FCSTD DOCUMENT  (FreeCAD 0.20R29177 (Git))
Label: Xpad_Top
License: All rights reserved
LicenseURL: http://en.wikipedia.org/wiki/All_rights_reserved
objects: Sketcher::SketchObject×1
note: 1 computed .brp shape members not serialized (recipe doc carries the construction recipe); baked Part::Feature solids carry a one-line shape summary decoded from their .brp

FEATURE [Sketcher::SketchObject] Sketch
  FullyConstrained = false
  sketch-geometry (36):
    g0: LineSegment StartX=0 StartY=47.625 StartZ=0 EndX=141.287 EndY=47.625 EndZ=0
    g1: LineSegment StartX=141.287 StartY=47.625 StartZ=0 EndX=141.287 EndY=0 EndZ=0
    g2: LineSegment StartX=141.287 StartY=0 StartZ=0 EndX=0 EndY=0 EndZ=0
    g3: LineSegment StartX=0 StartY=0 StartZ=0 EndX=0 EndY=47.625 EndZ=0
    g4: Circle CenterX=3.175 CenterY=3.175 CenterZ=0 NormalX=0 NormalY=0 NormalZ=1 AngleXU=0 Radius=1.5875
    g5: Circle CenterX=138.113 CenterY=3.175 CenterZ=0 NormalX=0 NormalY=0 NormalZ=1 AngleXU=0 Radius=1.5875
    g6: Circle CenterX=138.113 CenterY=44.45 CenterZ=0 NormalX=0 NormalY=0 NormalZ=1 AngleXU=0 Radius=1.5875
    g7: Circle CenterX=3.175 CenterY=44.45 CenterZ=0 NormalX=0 NormalY=0 NormalZ=1 AngleXU=0 Radius=1.5875
    g8: LineSegment StartX=1.90416 StartY=41.4018 StartZ=0 EndX=4.17658 EndY=41.4018 EndZ=0
    g9: LineSegment StartX=4.17658 StartY=41.4018 StartZ=0 EndX=4.17658 EndY=6.17209 EndZ=0
    g10: LineSegment StartX=4.17658 StartY=6.17209 StartZ=0 EndX=1.90416 EndY=6.17209 EndZ=0
    g11: LineSegment StartX=1.90416 StartY=6.17209 StartZ=0 EndX=1.90416 EndY=41.4018 EndZ=0
    g12: LineSegment StartX=136.92 StartY=40.3737 StartZ=0 EndX=139.308 EndY=40.3737 EndZ=0
    g13: LineSegment StartX=139.308 StartY=40.3737 StartZ=0 EndX=139.308 EndY=6.45346 EndZ=0
    g14: LineSegment StartX=139.308 StartY=6.45346 StartZ=0 EndX=136.92 EndY=6.45346 EndZ=0
    g15: LineSegment StartX=136.92 StartY=6.45346 StartZ=0 EndX=136.92 EndY=40.3737 EndZ=0
    g16: LineSegment StartX=14.7308 StartY=41.1364 StartZ=0 EndX=34.0334 EndY=41.1364 EndZ=0
    g17: LineSegment StartX=34.0334 StartY=41.1364 StartZ=0 EndX=34.0334 EndY=28.9277 EndZ=0
    g18: LineSegment StartX=34.0334 StartY=28.9277 StartZ=0 EndX=14.7308 EndY=28.9277 EndZ=0
    g19: LineSegment StartX=14.7308 StartY=28.9277 StartZ=0 EndX=14.7308 EndY=41.1364 EndZ=0
    g20: LineSegment StartX=39.354 StartY=40.5256 StartZ=0 EndX=53.7936 EndY=40.5256 EndZ=0
    g21: LineSegment StartX=53.7936 StartY=40.5256 StartZ=0 EndX=53.7936 EndY=7.69199 EndZ=0
    g22: LineSegment StartX=53.7936 StartY=7.69199 StartZ=0 EndX=39.354 EndY=7.69199 EndZ=0
    g23: LineSegment StartX=39.354 StartY=7.69199 StartZ=0 EndX=39.354 EndY=40.5256 EndZ=0
    g24: LineSegment StartX=60.189 StartY=41.726 StartZ=0 EndX=93.8065 EndY=41.726 EndZ=0
    g25: LineSegment StartX=93.8065 StartY=41.726 StartZ=0 EndX=93.8065 EndY=26.407 EndZ=0
    g26: LineSegment StartX=93.8065 StartY=26.407 StartZ=0 EndX=60.189 EndY=26.407 EndZ=0
    g27: LineSegment StartX=60.189 StartY=26.407 StartZ=0 EndX=60.189 EndY=41.726 EndZ=0
    g28: LineSegment StartX=108.536 StartY=19.2182 StartZ=0 EndX=129.304 EndY=19.2182 EndZ=0
    g29: LineSegment StartX=129.304 StartY=19.2182 StartZ=0 EndX=129.304 EndY=3.539 EndZ=0
    g30: LineSegment StartX=129.304 StartY=3.539 StartZ=0 EndX=108.536 EndY=3.539 EndZ=0
    g31: LineSegment StartX=108.536 StartY=3.539 StartZ=0 EndX=108.536 EndY=19.2182 EndZ=0
    g32: LineSegment StartX=94.9673 StartY=15.5272 StartZ=0 EndX=102.583 EndY=15.5272 EndZ=0
    g33: LineSegment StartX=102.583 StartY=15.5272 StartZ=0 EndX=102.583 EndY=7.94899 EndZ=0
    g34: LineSegment StartX=102.583 StartY=7.94899 StartZ=0 EndX=94.9673 EndY=7.94899 EndZ=0
    g35: LineSegment StartX=94.9673 StartY=7.94899 StartZ=0 EndX=94.9673 EndY=15.5272 EndZ=0
  constraints (79):
    c: Coincident(g0,g1)
    c: Coincident(g1,g2)
    c: Coincident(g2,g3)
    c: Coincident(g3,g0)
    c: Horizontal(g0)
    c: Horizontal(g2)
    c: Vertical(g1)
    c: Vertical(g3)
    c: Equal(g7,g4)
    c: Equal(g6,g5)
    c: Equal(g6,g7)
    c: Diameter(g7) = 3.175
    c: Horizontal(g7,g6)
    c: Vertical(g7,g4)
    c: Vertical(g5,g6)
    c: Horizontal(g4,g5)
    c: DistanceX(g7,g6) = 134.938
    c: DistanceX(g0,g7) = 3.175
    c: DistanceX(g6,g0) = 3.175
    c: DistanceY(g4,g7) = 41.275
    c: DistanceY(g2,g4) = 3.175
    c: DistanceY(g7,g0) = 3.175
    c: Coincident(g2,g-1)
    c: Coincident(g8,g9)
    c: Coincident(g9,g10)
    c: Coincident(g10,g11)
    c: Coincident(g11,g8)
    c: Horizontal(g8)
    c: Horizontal(g10)
    c: Vertical(g9)
    c: Vertical(g11)
    c: Coincident(g12,g13)
    c: Coincident(g13,g14)
    c: Coincident(g14,g15)
    c: Coincident(g15,g12)
    c: Horizontal(g12)
    c: Horizontal(g14)
    c: Vertical(g13)
    c: Vertical(g15)
    c: Coincident(g16,g17)
    c: Coincident(g17,g18)
    c: Coincident(g18,g19)
    c: Coincident(g19,g16)
    c: Horizontal(g16)
    c: Horizontal(g18)
    c: Vertical(g17)
    c: Vertical(g19)
    c: Coincident(g20,g21)
    c: Coincident(g21,g22)
    c: Coincident(g22,g23)
    c: Coincident(g23,g20)
    c: Horizontal(g20)
    c: Horizontal(g22)
    c: Vertical(g21)
    c: Vertical(g23)
    c: Coincident(g24,g25)
    c: Coincident(g25,g26)
    c: Coincident(g26,g27)
    c: Coincident(g27,g24)
    c: Horizontal(g24)
    c: Horizontal(g26)
    c: Vertical(g25)
    c: Vertical(g27)
    c: Coincident(g28,g29)
    c: Coincident(g29,g30)
    c: Coincident(g30,g31)
    c: Coincident(g31,g28)
    c: Horizontal(g28)
    c: Horizontal(g30)
    c: Vertical(g29)
    c: Vertical(g31)
    c: Coincident(g32,g33)
    c: Coincident(g33,g34)
    c: Coincident(g34,g35)
    c: Coincident(g35,g32)
    c: Horizontal(g32)
    c: Horizontal(g34)
    c: Vertical(g33)
    c: Vertical(g35)
